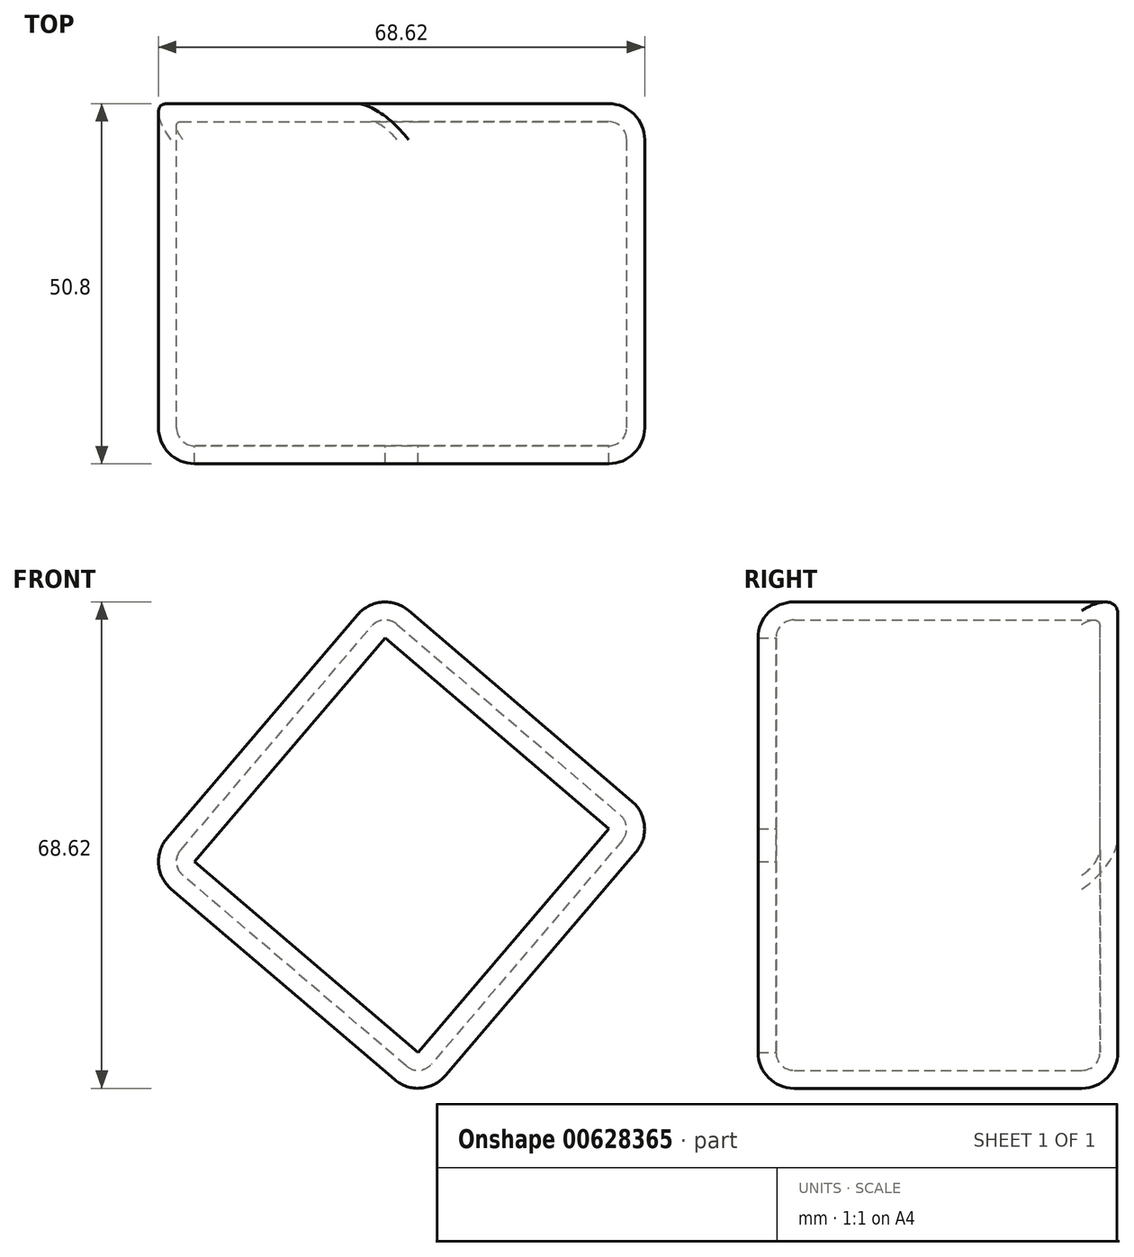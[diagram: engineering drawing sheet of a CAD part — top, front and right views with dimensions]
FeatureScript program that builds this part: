
annotation { "Feature Type Name" : "Feature", "Feature Type Description" : "" }
export const myFeature = defineFeature(function(context is Context, id is Id, definition is map)
    precondition{}
    {
        {
            var Q0;
            Q0=qCreatedBy(makeId("Front.planeOp"),FACE);
            var sketch = newSketch(context, id + "F0", { "sketchPlane" : qUnion([Q0])});
            skCircle(sketch, "E0.cCircle", {"center": v(0, 0) * mm, "radius": 25.81 * mm, "construction": true});
            skLineSegment(sketch, "E0.0", {"start": v(2.88, -36.39) * mm, "end": v(-36.39, -2.88) * mm});
            skLineSegment(sketch, "E0.1", {"start": v(-36.39, -2.88) * mm, "end": v(-2.88, 36.39) * mm});
            skLineSegment(sketch, "E0.2", {"start": v(-2.88, 36.39) * mm, "end": v(36.39, 2.88) * mm});
            skLineSegment(sketch, "E0.3", {"start": v(36.39, 2.88) * mm, "end": v(2.88, -36.39) * mm});
            skPoint(sketch, "E0.0.midPoint", {"position": v(-16.75, -19.64) * mm});
            skSolve(sketch);
        }
        {
            var Q0;
            Q0=makeQuery(id+"F0.imprint","IMPRINT",FACE,{"disambiguationData":[TD([[makeQuery(id+"F0.imprint","IMPRINT",EDGE,{"derivedFrom":sQuery(id+"F0.wireOp",EDGE,"E0.0")}),-1.0]])]});
            extrude(context, id + "F1", {"entities" : qUnion([Q0]), "depth" : 50.8 * mm, "offsetDistance" : 25.4 * mm});
        }
        {
            var Q0;
            Q0=makeQuery(id+"F1.opExtrude","SWEPT_FACE",FACE,{"disambiguationData":[OSD([sQuery(id+"F0.wireOp",EDGE,"E0.2")])]});
            var Q1;
            Q1=makeQuery(id+"F1.opExtrude","CAP_FACE",FACE,{"disambiguationData":[OSD([sQuery(id+"F0.wireOp",EDGE,"E0.0"),sQuery(id+"F0.wireOp",EDGE,"E0.1"),sQuery(id+"F0.wireOp",EDGE,"E0.2"),sQuery(id+"F0.wireOp",EDGE,"E0.3")])],"isStart":false});
            var Q2;
            Q2=makeQuery(id+"F1.opExtrude","SWEPT_FACE",FACE,{"disambiguationData":[OSD([sQuery(id+"F0.wireOp",EDGE,"E0.3")])]});
            var Q3;
            Q3=makeQuery(id+"F1.opExtrude","SWEPT_FACE",FACE,{"disambiguationData":[OSD([sQuery(id+"F0.wireOp",EDGE,"E0.0")])]});
            fillet(context, id + "F2", {"entities" : qUnion([Q0, Q1, Q2, Q3]), "radius" : 5.08 * mm, "tangentPropagation" : true, "allowEdgeOverflow" : false});
        }
        {
            var Q0;
            Q0=makeQuery(id+"F1.opExtrude","CAP_FACE",FACE,{"disambiguationData":[OSD([sQuery(id+"F0.wireOp",EDGE,"E0.0"),sQuery(id+"F0.wireOp",EDGE,"E0.1"),sQuery(id+"F0.wireOp",EDGE,"E0.2"),sQuery(id+"F0.wireOp",EDGE,"E0.3")])],"isStart":false});
            shell(context, id + "F3", {"entities" : qUnion([Q0]), "thickness" : 2.54 * mm});
        }
    });
